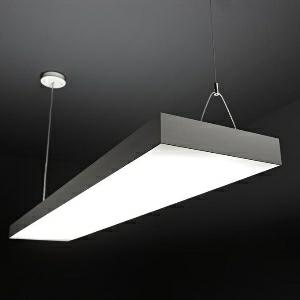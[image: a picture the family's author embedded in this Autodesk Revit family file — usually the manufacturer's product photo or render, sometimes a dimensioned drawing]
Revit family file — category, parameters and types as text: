
# Revit family: spectral_norea_norea-p_1545_13770_840_mps_a2fc
name_source: partatom
category: Lighting Fixtures
revit_build: Autodesk Revit 2016 (Build: 20150220_1215(x64)
units: mm (PartAtom-declared; Revit-internal decimal feet)

## family parameters
Cut with Voids When Loaded = No
Host = Face
Light Source = No
Part Type = Normal
Room Calculation Point = No
Round Connector Dimension = Use Diameter
Shared = No

## types (1)
- SPECTRAL NOREA (1 x )
    Apparent Load = 0 VA
    Approval mark = CE
    CIE Flux Codes = 72 93 98 75 75
    Control Gear = Electronic transformer
    Default Elevation = 1800 mm
    Description = SPT0000095
NOREA Pendant luminaire

Design:
Square luminaire element with a microprism panel in a natural anodised aluminium profile frame surround. The luminaire is suspended by a wire pendant with ceiling holder and transparent connecting cable with rectangular powder-coated ceiling junction box. Cable length adjustable at the junction box, steel wire steplessly height adjustable at the luminaire. The electrical gear is accommodated under a cover at the top of the luminaire. This can be removed using key holes for maintenance work. The indirect component for brightening the ceiling is provided by LED linear modules at the top of the luminaire. The LED module is formed as a rectangular LED flat board. Luminaire with heat-resistant wiring. Variant suitable for office use with a microprism panel MPS. The LED points are visible as circles on the microprism panel. Also in a dimmable version.

Colour:
Housing – similar to RAL 9016 White silk matt;
Frame – natural anodised
    Height = 50 mm
    Lamp = 1 x
    Lamp count = 1
    Length = 1545 mm
    Luminous efficacy = 0 lm/W
    Manufacturer = Ridi
    ModVariant = No
    Model = NOREA-P 1545/13770/840 MPS
    Mounting Place = Ceiling
    Mounting Type = Pendant
    Number of Poles = 1
    OnlyDefault = Yes
    Power Factor = 1
    Product Name = SPECTRAL NOREA
    Product group = Pendant luminaire
    ProductGroupID = 9
    Protection Class = Protection class
    Protection Degree = IP 20
    RlxData = <blob elided: 40713 chars, md5=6f3ed41a>
    Socket = socket
    Standby Power = 0 W
    System Light Flux = 0 lm
    System Power = 0 W
    Type Image = norea01.jpg
    URL = http://reluxnet.relux.com
    VarID = 1
    Voltage = 0 V
    Weight = 0.00 kg
    Width = 312 mm

## geometry (parser evidence)
native form markers: Sweep x12
no freeform markers — native parametric forms only
